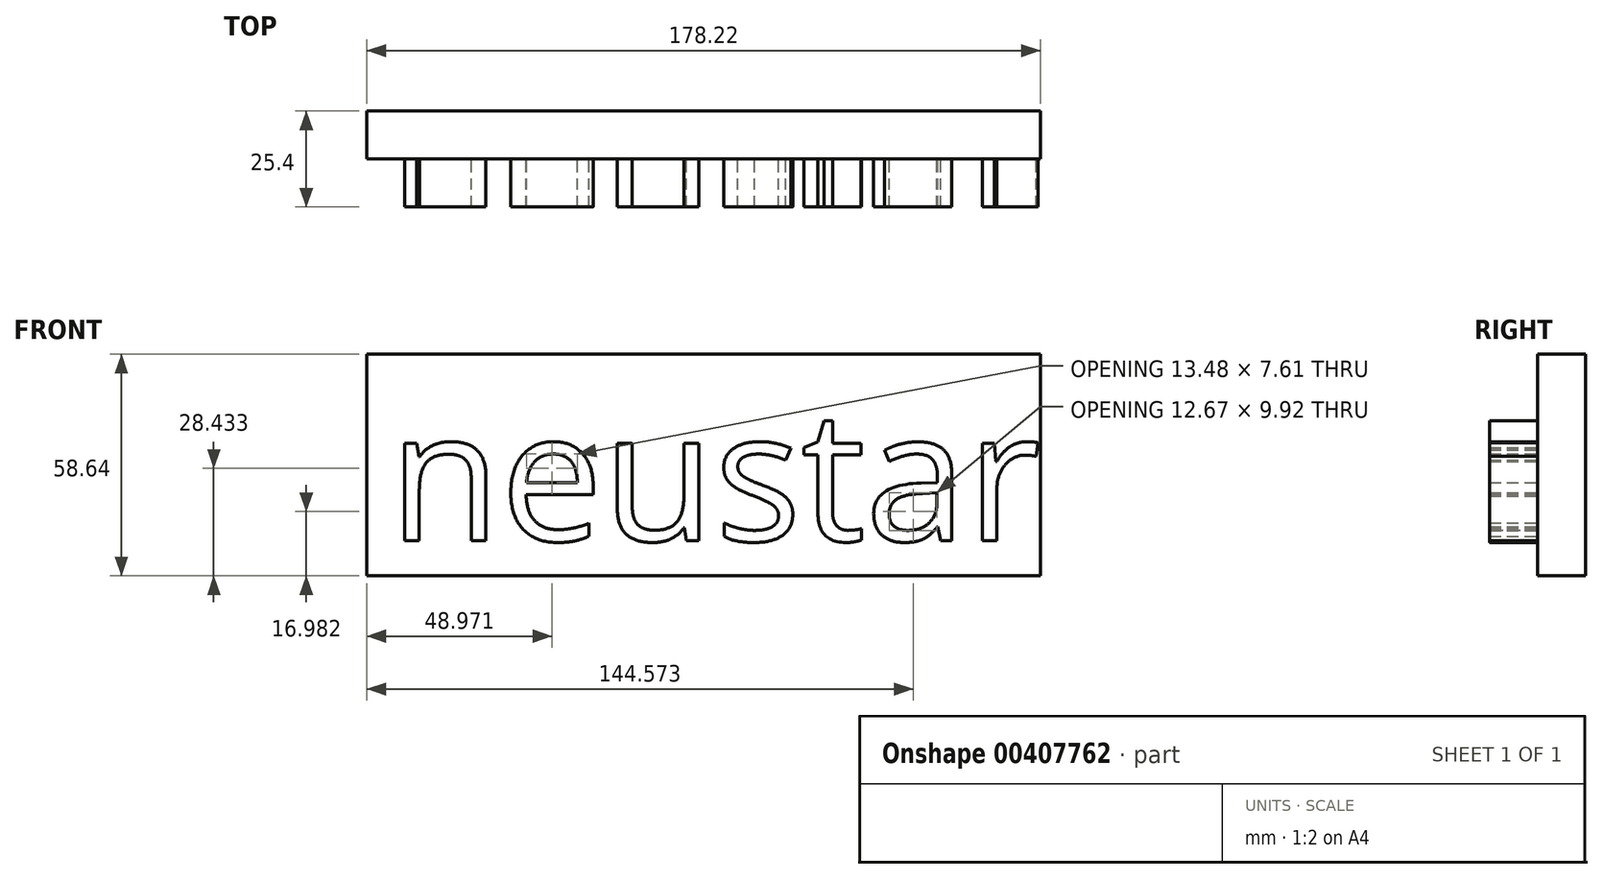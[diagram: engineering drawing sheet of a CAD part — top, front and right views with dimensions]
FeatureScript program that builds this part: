
annotation { "Feature Type Name" : "Feature", "Feature Type Description" : "" }
export const myFeature = defineFeature(function(context is Context, id is Id, definition is map)
    precondition{}
    {
        {
            var Q0;
            Q0=qCreatedBy(makeId("Front.planeOp"),FACE);
            var sketch = newSketch(context, id + "F0", { "sketchPlane" : qUnion([Q0])});
            skText(sketch, "E0", { "text": "neustar", "fontName": "OpenSans-Regular.ttf"});
            const initialGuessF0  = {"E0": [-0.04371, -0.00969, 1, 0, 0.03467]};
            skSetInitialGuess(sketch, initialGuessF0);
            skSolve(sketch);
        }
        {
            var Q0;
            Q0 = qSketchRegion(id + "F0", true);
            extrude(context, id + "F1", {"entities" : qUnion([Q0]), "depth" : 12.7 * mm});
        }
        {
            var Q0;
            Q0=qCreatedBy(makeId("Front.planeOp"),FACE);
            var sketch = newSketch(context, id + "F2", { "sketchPlane" : qUnion([Q0])});
            skLineSegment(sketch, "E1.bottom", {"start": v(128.67, 39.68) * mm, "end": v(-49.55, 39.68) * mm});
            skLineSegment(sketch, "E1.top", {"start": v(128.67, -18.96) * mm, "end": v(-49.55, -18.96) * mm});
            skLineSegment(sketch, "E1.left", {"start": v(128.67, 39.68) * mm, "end": v(128.67, -18.96) * mm});
            skLineSegment(sketch, "E1.right", {"start": v(-49.55, 39.68) * mm, "end": v(-49.55, -18.96) * mm});
            skSolve(sketch);
        }
        {
            var Q0;
            Q0 = qSketchRegion(id + "F2", true);
            extrude(context, id + "F3", {"entities" : qUnion([Q0]), "oppositeDirection" : true, "depth" : 12.7 * mm});
        }
    });
